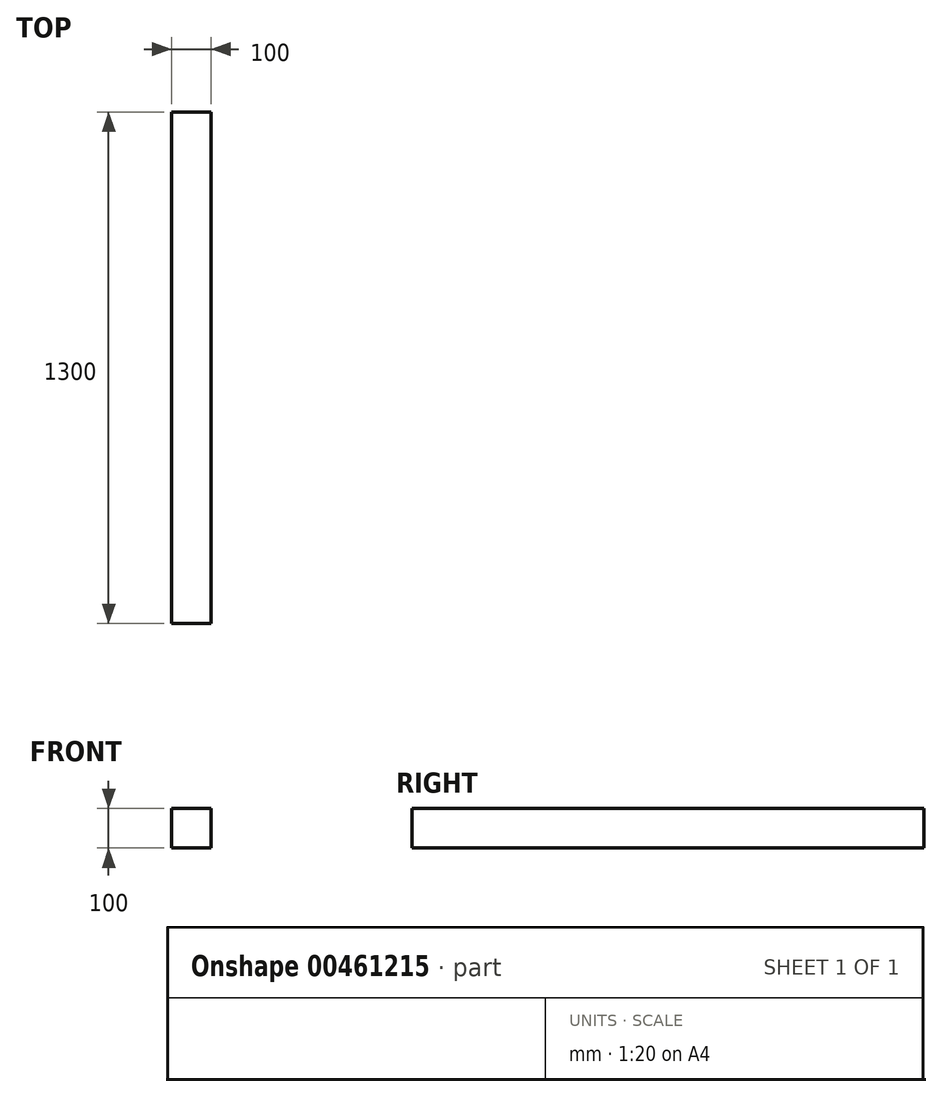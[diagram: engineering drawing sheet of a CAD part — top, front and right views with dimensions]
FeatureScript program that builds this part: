
annotation { "Feature Type Name" : "Feature", "Feature Type Description" : "" }
export const myFeature = defineFeature(function(context is Context, id is Id, definition is map)
    precondition{}
    {
        {
            var Q0;
            Q0=qCreatedBy(makeId("Front.planeOp"),FACE);
            var sketch = newSketch(context, id + "F0", { "sketchPlane" : qUnion([Q0])});
            skLineSegment(sketch, "E0.bottom", {"start": v(0, 0) * mm, "end": v(100, 0) * mm});
            skLineSegment(sketch, "E0.top", {"start": v(0, 100) * mm, "end": v(100, 100) * mm});
            skLineSegment(sketch, "E0.left", {"start": v(0, 0) * mm, "end": v(0, 100) * mm});
            skLineSegment(sketch, "E0.right", {"start": v(100, 0) * mm, "end": v(100, 100) * mm});
            skSolve(sketch);
        }
        {
            var Q0;
            Q0 = qSketchRegion(id + "F0", true);
            extrude(context, id + "F1", {"entities" : qUnion([Q0]), "depth" : 1300 * mm});
        }
    });
